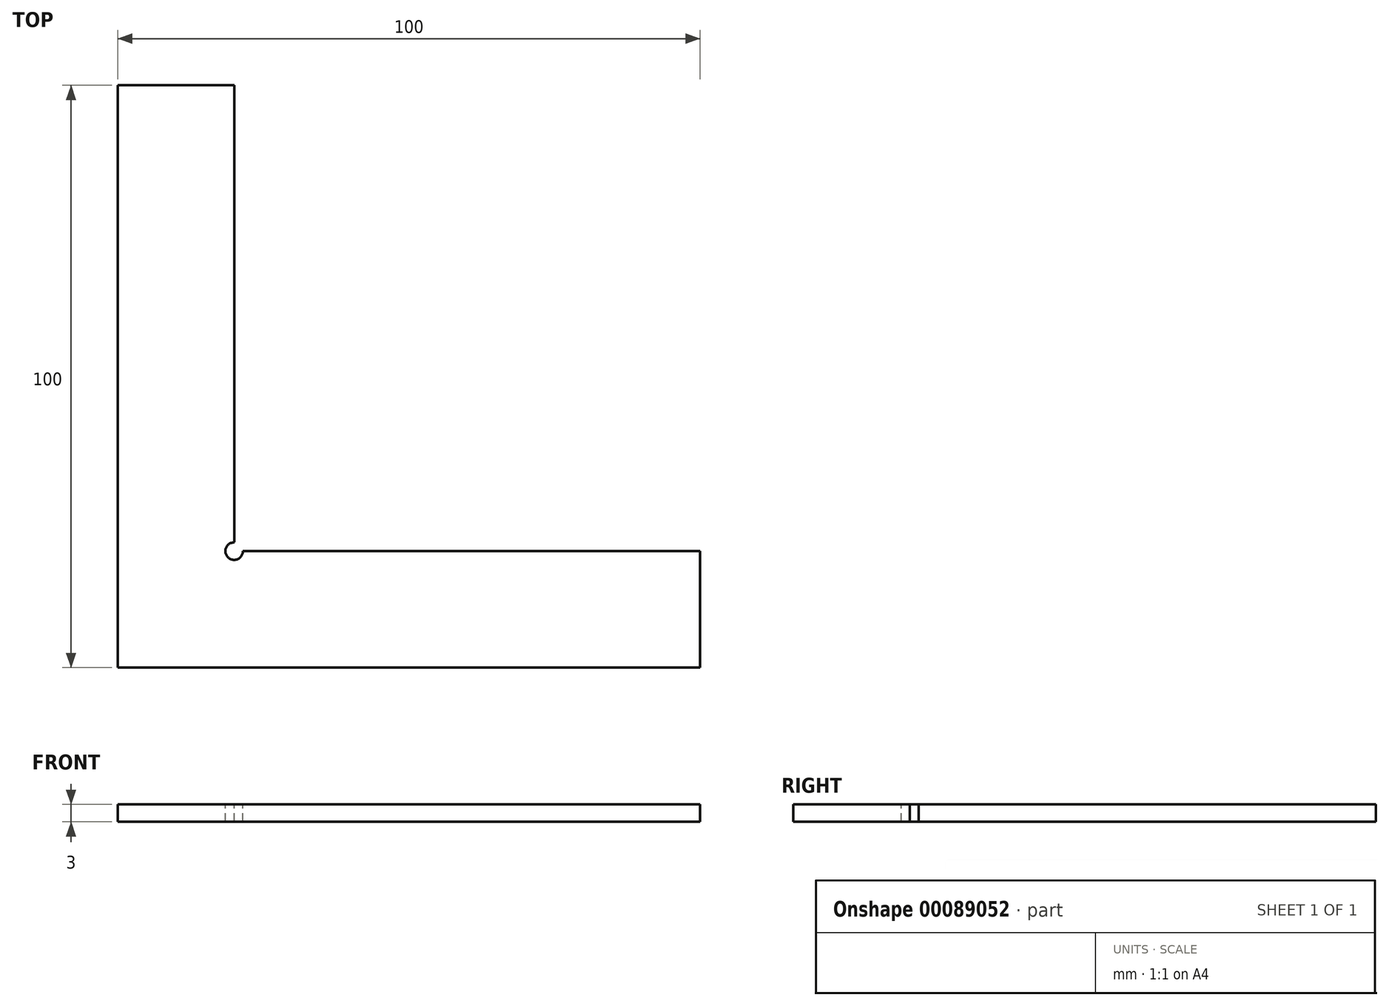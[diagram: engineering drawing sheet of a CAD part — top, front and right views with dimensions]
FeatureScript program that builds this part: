
annotation { "Feature Type Name" : "Feature", "Feature Type Description" : "" }
export const myFeature = defineFeature(function(context is Context, id is Id, definition is map)
    precondition{}
    {
        {
            var Q0;
            Q0=qCreatedBy(makeId("Top.planeOp"),FACE);
            var sketch = newSketch(context, id + "F0", { "sketchPlane" : qUnion([Q0])});
            skLineSegment(sketch, "E0", {"start": v(0, 0) * mm, "end": v(100, 0) * mm});
            skLineSegment(sketch, "E1", {"start": v(100, 0) * mm, "end": v(100, 20) * mm});
            skLineSegment(sketch, "E2", {"start": v(100, 20) * mm, "end": v(22, 20) * mm});
            skLineSegment(sketch, "E3", {"start": v(20, 20) * mm, "end": v(20, 22) * mm});
            skLineSegment(sketch, "E4", {"start": v(20, 100) * mm, "end": v(0, 100) * mm});
            skLineSegment(sketch, "E5", {"start": v(0, 100) * mm, "end": v(0, 0) * mm});
            skArc(sketch, "E6", {"start": v(20, 21.5) * mm, "mid": v(18.94, 18.94) * mm, "end": v(21.5, 20) * mm});
            skLineSegment(sketch, "E7", {"start": v(20, 18.5) * mm, "end": v(20, 15) * mm});
            skLineSegment(sketch, "E8", {"start": v(21, 20) * mm, "end": v(21, 19) * mm});
            skLineSegment(sketch, "E9.1.0.0", {"start": v(22, 20) * mm, "end": v(22, 19) * mm});
            skLineSegment(sketch, "E9.2.0.0", {"start": v(23, 20) * mm, "end": v(23, 19) * mm});
            skLineSegment(sketch, "E9.3.0.0", {"start": v(24, 20) * mm, "end": v(24, 19) * mm});
            skLineSegment(sketch, "E9.direction1", {"start": v(21, 19) * mm, "end": v(22, 19) * mm, "construction": true});
            skLineSegment(sketch, "E10.1.0.0", {"start": v(25, 20) * mm, "end": v(25, 15) * mm});
            skLineSegment(sketch, "E10.1.0.1", {"start": v(26, 20) * mm, "end": v(26, 19) * mm});
            skLineSegment(sketch, "E10.1.0.2", {"start": v(27, 20) * mm, "end": v(27, 19) * mm});
            skLineSegment(sketch, "E10.1.0.3", {"start": v(28, 20) * mm, "end": v(28, 19) * mm});
            skLineSegment(sketch, "E10.1.0.4", {"start": v(29, 20) * mm, "end": v(29, 19) * mm});
            skLineSegment(sketch, "E10.2.0.0", {"start": v(30, 20) * mm, "end": v(30, 15) * mm});
            skLineSegment(sketch, "E10.2.0.1", {"start": v(31, 20) * mm, "end": v(31, 19) * mm});
            skLineSegment(sketch, "E10.2.0.2", {"start": v(32, 20) * mm, "end": v(32, 19) * mm});
            skLineSegment(sketch, "E10.2.0.3", {"start": v(33, 20) * mm, "end": v(33, 19) * mm});
            skLineSegment(sketch, "E10.2.0.4", {"start": v(34, 20) * mm, "end": v(34, 19) * mm});
            skLineSegment(sketch, "E10.3.0.0", {"start": v(35, 20) * mm, "end": v(35, 15) * mm});
            skLineSegment(sketch, "E10.3.0.1", {"start": v(36, 20) * mm, "end": v(36, 19) * mm});
            skLineSegment(sketch, "E10.3.0.2", {"start": v(37, 20) * mm, "end": v(37, 19) * mm});
            skLineSegment(sketch, "E10.3.0.3", {"start": v(38, 20) * mm, "end": v(38, 19) * mm});
            skLineSegment(sketch, "E10.3.0.4", {"start": v(39, 20) * mm, "end": v(39, 19) * mm});
            skLineSegment(sketch, "E10.4.0.0", {"start": v(40, 20) * mm, "end": v(40, 15) * mm});
            skLineSegment(sketch, "E10.4.0.1", {"start": v(41, 20) * mm, "end": v(41, 19) * mm});
            skLineSegment(sketch, "E10.4.0.2", {"start": v(42, 20) * mm, "end": v(42, 19) * mm});
            skLineSegment(sketch, "E10.4.0.3", {"start": v(43, 20) * mm, "end": v(43, 19) * mm});
            skLineSegment(sketch, "E10.4.0.4", {"start": v(44, 20) * mm, "end": v(44, 19) * mm});
            skLineSegment(sketch, "E10.5.0.0", {"start": v(45, 20) * mm, "end": v(45, 15) * mm});
            skLineSegment(sketch, "E10.5.0.1", {"start": v(46, 20) * mm, "end": v(46, 19) * mm});
            skLineSegment(sketch, "E10.5.0.2", {"start": v(47, 20) * mm, "end": v(47, 19) * mm});
            skLineSegment(sketch, "E10.5.0.3", {"start": v(48, 20) * mm, "end": v(48, 19) * mm});
            skLineSegment(sketch, "E10.5.0.4", {"start": v(49, 20) * mm, "end": v(49, 19) * mm});
            skLineSegment(sketch, "E10.6.0.0", {"start": v(50, 20) * mm, "end": v(50, 15) * mm});
            skLineSegment(sketch, "E10.6.0.1", {"start": v(51, 20) * mm, "end": v(51, 19) * mm});
            skLineSegment(sketch, "E10.6.0.2", {"start": v(52, 20) * mm, "end": v(52, 19) * mm});
            skLineSegment(sketch, "E10.6.0.3", {"start": v(53, 20) * mm, "end": v(53, 19) * mm});
            skLineSegment(sketch, "E10.6.0.4", {"start": v(54, 20) * mm, "end": v(54, 19) * mm});
            skLineSegment(sketch, "E10.7.0.0", {"start": v(55, 20) * mm, "end": v(55, 15) * mm});
            skLineSegment(sketch, "E10.7.0.1", {"start": v(56, 20) * mm, "end": v(56, 19) * mm});
            skLineSegment(sketch, "E10.7.0.2", {"start": v(57, 20) * mm, "end": v(57, 19) * mm});
            skLineSegment(sketch, "E10.7.0.3", {"start": v(58, 20) * mm, "end": v(58, 19) * mm});
            skLineSegment(sketch, "E10.7.0.4", {"start": v(59, 20) * mm, "end": v(59, 19) * mm});
            skLineSegment(sketch, "E10.8.0.0", {"start": v(60, 20) * mm, "end": v(60, 15) * mm});
            skLineSegment(sketch, "E10.8.0.1", {"start": v(61, 20) * mm, "end": v(61, 19) * mm});
            skLineSegment(sketch, "E10.8.0.2", {"start": v(62, 20) * mm, "end": v(62, 19) * mm});
            skLineSegment(sketch, "E10.8.0.3", {"start": v(63, 20) * mm, "end": v(63, 19) * mm});
            skLineSegment(sketch, "E10.8.0.4", {"start": v(64, 20) * mm, "end": v(64, 19) * mm});
            skLineSegment(sketch, "E10.9.0.0", {"start": v(65, 20) * mm, "end": v(65, 15) * mm});
            skLineSegment(sketch, "E10.9.0.1", {"start": v(66, 20) * mm, "end": v(66, 19) * mm});
            skLineSegment(sketch, "E10.9.0.2", {"start": v(67, 20) * mm, "end": v(67, 19) * mm});
            skLineSegment(sketch, "E10.9.0.3", {"start": v(68, 20) * mm, "end": v(68, 19) * mm});
            skLineSegment(sketch, "E10.9.0.4", {"start": v(69, 20) * mm, "end": v(69, 19) * mm});
            skLineSegment(sketch, "E10.10.0.0", {"start": v(70, 20) * mm, "end": v(70, 15) * mm});
            skLineSegment(sketch, "E10.10.0.1", {"start": v(71, 20) * mm, "end": v(71, 19) * mm});
            skLineSegment(sketch, "E10.10.0.2", {"start": v(72, 20) * mm, "end": v(72, 19) * mm});
            skLineSegment(sketch, "E10.10.0.3", {"start": v(73, 20) * mm, "end": v(73, 19) * mm});
            skLineSegment(sketch, "E10.10.0.4", {"start": v(74, 20) * mm, "end": v(74, 19) * mm});
            skLineSegment(sketch, "E10.11.0.0", {"start": v(75, 20) * mm, "end": v(75, 15) * mm});
            skLineSegment(sketch, "E10.11.0.1", {"start": v(76, 20) * mm, "end": v(76, 19) * mm});
            skLineSegment(sketch, "E10.11.0.2", {"start": v(77, 20) * mm, "end": v(77, 19) * mm});
            skLineSegment(sketch, "E10.11.0.3", {"start": v(78, 20) * mm, "end": v(78, 19) * mm});
            skLineSegment(sketch, "E10.11.0.4", {"start": v(79, 20) * mm, "end": v(79, 19) * mm});
            skLineSegment(sketch, "E10.12.0.0", {"start": v(80, 20) * mm, "end": v(80, 15) * mm});
            skLineSegment(sketch, "E10.12.0.1", {"start": v(81, 20) * mm, "end": v(81, 19) * mm});
            skLineSegment(sketch, "E10.12.0.2", {"start": v(82, 20) * mm, "end": v(82, 19) * mm});
            skLineSegment(sketch, "E10.12.0.3", {"start": v(83, 20) * mm, "end": v(83, 19) * mm});
            skLineSegment(sketch, "E10.12.0.4", {"start": v(84, 20) * mm, "end": v(84, 19) * mm});
            skLineSegment(sketch, "E10.13.0.0", {"start": v(85, 20) * mm, "end": v(85, 15) * mm});
            skLineSegment(sketch, "E10.13.0.1", {"start": v(86, 20) * mm, "end": v(86, 19) * mm});
            skLineSegment(sketch, "E10.13.0.2", {"start": v(87, 20) * mm, "end": v(87, 19) * mm});
            skLineSegment(sketch, "E10.13.0.3", {"start": v(88, 20) * mm, "end": v(88, 19) * mm});
            skLineSegment(sketch, "E10.13.0.4", {"start": v(89, 20) * mm, "end": v(89, 19) * mm});
            skLineSegment(sketch, "E10.14.0.0", {"start": v(90, 20) * mm, "end": v(90, 15) * mm});
            skLineSegment(sketch, "E10.14.0.1", {"start": v(91, 20) * mm, "end": v(91, 19) * mm});
            skLineSegment(sketch, "E10.14.0.2", {"start": v(92, 20) * mm, "end": v(92, 19) * mm});
            skLineSegment(sketch, "E10.14.0.3", {"start": v(93, 20) * mm, "end": v(93, 19) * mm});
            skLineSegment(sketch, "E10.14.0.4", {"start": v(94, 20) * mm, "end": v(94, 19) * mm});
            skLineSegment(sketch, "E10.direction1", {"start": v(20, 15) * mm, "end": v(25, 15) * mm, "construction": true});
            skLineSegment(sketch, "E11.0.15.0", {"start": v(95, 20) * mm, "end": v(95, 15) * mm});
            skLineSegment(sketch, "E11.3.15.0", {"start": v(96, 20) * mm, "end": v(96, 19) * mm});
            skLineSegment(sketch, "E11.6.15.0", {"start": v(97, 20) * mm, "end": v(97, 19) * mm});
            skLineSegment(sketch, "E11.9.15.0", {"start": v(98, 20) * mm, "end": v(98, 19) * mm});
            skLineSegment(sketch, "E11.12.15.0", {"start": v(99, 20) * mm, "end": v(99, 19) * mm});
            skLineSegment(sketch, "E12", {"start": v(18.5, 20) * mm, "end": v(15, 20) * mm});
            skLineSegment(sketch, "E13", {"start": v(20, 21) * mm, "end": v(19, 21) * mm});
            skLineSegment(sketch, "E14.1.0.0", {"start": v(20, 22) * mm, "end": v(19, 22) * mm});
            skLineSegment(sketch, "E14.2.0.0", {"start": v(20, 23) * mm, "end": v(19, 23) * mm});
            skLineSegment(sketch, "E14.3.0.0", {"start": v(20, 24) * mm, "end": v(19, 24) * mm});
            skLineSegment(sketch, "E14.direction1", {"start": v(19, 21) * mm, "end": v(19, 22) * mm, "construction": true});
            skLineSegment(sketch, "E15.1.0.0", {"start": v(20, 25) * mm, "end": v(15, 25) * mm});
            skLineSegment(sketch, "E15.1.0.1", {"start": v(20, 26) * mm, "end": v(19, 26) * mm});
            skLineSegment(sketch, "E15.1.0.2", {"start": v(20, 27) * mm, "end": v(19, 27) * mm});
            skLineSegment(sketch, "E15.1.0.3", {"start": v(20, 28) * mm, "end": v(19, 28) * mm});
            skLineSegment(sketch, "E15.1.0.4", {"start": v(20, 29) * mm, "end": v(19, 29) * mm});
            skLineSegment(sketch, "E15.2.0.0", {"start": v(20, 30) * mm, "end": v(15, 30) * mm});
            skLineSegment(sketch, "E15.2.0.1", {"start": v(20, 31) * mm, "end": v(19, 31) * mm});
            skLineSegment(sketch, "E15.2.0.2", {"start": v(20, 32) * mm, "end": v(19, 32) * mm});
            skLineSegment(sketch, "E15.2.0.3", {"start": v(20, 33) * mm, "end": v(19, 33) * mm});
            skLineSegment(sketch, "E15.2.0.4", {"start": v(20, 34) * mm, "end": v(19, 34) * mm});
            skLineSegment(sketch, "E15.3.0.0", {"start": v(20, 35) * mm, "end": v(15, 35) * mm});
            skLineSegment(sketch, "E15.3.0.1", {"start": v(20, 36) * mm, "end": v(19, 36) * mm});
            skLineSegment(sketch, "E15.3.0.2", {"start": v(20, 37) * mm, "end": v(19, 37) * mm});
            skLineSegment(sketch, "E15.3.0.3", {"start": v(20, 38) * mm, "end": v(19, 38) * mm});
            skLineSegment(sketch, "E15.3.0.4", {"start": v(20, 39) * mm, "end": v(19, 39) * mm});
            skLineSegment(sketch, "E15.4.0.0", {"start": v(20, 40) * mm, "end": v(15, 40) * mm});
            skLineSegment(sketch, "E15.4.0.1", {"start": v(20, 41) * mm, "end": v(19, 41) * mm});
            skLineSegment(sketch, "E15.4.0.2", {"start": v(20, 42) * mm, "end": v(19, 42) * mm});
            skLineSegment(sketch, "E15.4.0.3", {"start": v(20, 43) * mm, "end": v(19, 43) * mm});
            skLineSegment(sketch, "E15.4.0.4", {"start": v(20, 44) * mm, "end": v(19, 44) * mm});
            skLineSegment(sketch, "E15.5.0.0", {"start": v(20, 45) * mm, "end": v(15, 45) * mm});
            skLineSegment(sketch, "E15.5.0.1", {"start": v(20, 46) * mm, "end": v(19, 46) * mm});
            skLineSegment(sketch, "E15.5.0.2", {"start": v(20, 47) * mm, "end": v(19, 47) * mm});
            skLineSegment(sketch, "E15.5.0.3", {"start": v(20, 48) * mm, "end": v(19, 48) * mm});
            skLineSegment(sketch, "E15.5.0.4", {"start": v(20, 49) * mm, "end": v(19, 49) * mm});
            skLineSegment(sketch, "E15.6.0.0", {"start": v(20, 50) * mm, "end": v(15, 50) * mm});
            skLineSegment(sketch, "E15.6.0.1", {"start": v(20, 51) * mm, "end": v(19, 51) * mm});
            skLineSegment(sketch, "E15.6.0.2", {"start": v(20, 52) * mm, "end": v(19, 52) * mm});
            skLineSegment(sketch, "E15.6.0.3", {"start": v(20, 53) * mm, "end": v(19, 53) * mm});
            skLineSegment(sketch, "E15.6.0.4", {"start": v(20, 54) * mm, "end": v(19, 54) * mm});
            skLineSegment(sketch, "E15.7.0.0", {"start": v(20, 55) * mm, "end": v(15, 55) * mm});
            skLineSegment(sketch, "E15.7.0.1", {"start": v(20, 56) * mm, "end": v(19, 56) * mm});
            skLineSegment(sketch, "E15.7.0.2", {"start": v(20, 57) * mm, "end": v(19, 57) * mm});
            skLineSegment(sketch, "E15.7.0.3", {"start": v(20, 58) * mm, "end": v(19, 58) * mm});
            skLineSegment(sketch, "E15.7.0.4", {"start": v(20, 59) * mm, "end": v(19, 59) * mm});
            skLineSegment(sketch, "E15.8.0.0", {"start": v(20, 60) * mm, "end": v(15, 60) * mm});
            skLineSegment(sketch, "E15.8.0.1", {"start": v(20, 61) * mm, "end": v(19, 61) * mm});
            skLineSegment(sketch, "E15.8.0.2", {"start": v(20, 62) * mm, "end": v(19, 62) * mm});
            skLineSegment(sketch, "E15.8.0.3", {"start": v(20, 63) * mm, "end": v(19, 63) * mm});
            skLineSegment(sketch, "E15.8.0.4", {"start": v(20, 64) * mm, "end": v(19, 64) * mm});
            skLineSegment(sketch, "E15.9.0.0", {"start": v(20, 65) * mm, "end": v(15, 65) * mm});
            skLineSegment(sketch, "E15.9.0.1", {"start": v(20, 66) * mm, "end": v(19, 66) * mm});
            skLineSegment(sketch, "E15.9.0.2", {"start": v(20, 67) * mm, "end": v(19, 67) * mm});
            skLineSegment(sketch, "E15.9.0.3", {"start": v(20, 68) * mm, "end": v(19, 68) * mm});
            skLineSegment(sketch, "E15.9.0.4", {"start": v(20, 69) * mm, "end": v(19, 69) * mm});
            skLineSegment(sketch, "E15.10.0.0", {"start": v(20, 70) * mm, "end": v(15, 70) * mm});
            skLineSegment(sketch, "E15.10.0.1", {"start": v(20, 71) * mm, "end": v(19, 71) * mm});
            skLineSegment(sketch, "E15.10.0.2", {"start": v(20, 72) * mm, "end": v(19, 72) * mm});
            skLineSegment(sketch, "E15.10.0.3", {"start": v(20, 73) * mm, "end": v(19, 73) * mm});
            skLineSegment(sketch, "E15.10.0.4", {"start": v(20, 74) * mm, "end": v(19, 74) * mm});
            skLineSegment(sketch, "E15.11.0.0", {"start": v(20, 75) * mm, "end": v(15, 75) * mm});
            skLineSegment(sketch, "E15.11.0.1", {"start": v(20, 76) * mm, "end": v(19, 76) * mm});
            skLineSegment(sketch, "E15.11.0.2", {"start": v(20, 77) * mm, "end": v(19, 77) * mm});
            skLineSegment(sketch, "E15.11.0.3", {"start": v(20, 78) * mm, "end": v(19, 78) * mm});
            skLineSegment(sketch, "E15.11.0.4", {"start": v(20, 79) * mm, "end": v(19, 79) * mm});
            skLineSegment(sketch, "E15.12.0.0", {"start": v(20, 80) * mm, "end": v(15, 80) * mm});
            skLineSegment(sketch, "E15.12.0.1", {"start": v(20, 81) * mm, "end": v(19, 81) * mm});
            skLineSegment(sketch, "E15.12.0.2", {"start": v(20, 82) * mm, "end": v(19, 82) * mm});
            skLineSegment(sketch, "E15.12.0.3", {"start": v(20, 83) * mm, "end": v(19, 83) * mm});
            skLineSegment(sketch, "E15.12.0.4", {"start": v(20, 84) * mm, "end": v(19, 84) * mm});
            skLineSegment(sketch, "E15.13.0.0", {"start": v(20, 85) * mm, "end": v(15, 85) * mm});
            skLineSegment(sketch, "E15.13.0.1", {"start": v(20, 86) * mm, "end": v(19, 86) * mm});
            skLineSegment(sketch, "E15.13.0.2", {"start": v(20, 87) * mm, "end": v(19, 87) * mm});
            skLineSegment(sketch, "E15.13.0.3", {"start": v(20, 88) * mm, "end": v(19, 88) * mm});
            skLineSegment(sketch, "E15.13.0.4", {"start": v(20, 89) * mm, "end": v(19, 89) * mm});
            skLineSegment(sketch, "E15.14.0.0", {"start": v(20, 90) * mm, "end": v(15, 90) * mm});
            skLineSegment(sketch, "E15.14.0.1", {"start": v(20, 91) * mm, "end": v(19, 91) * mm});
            skLineSegment(sketch, "E15.14.0.2", {"start": v(20, 92) * mm, "end": v(19, 92) * mm});
            skLineSegment(sketch, "E15.14.0.3", {"start": v(20, 93) * mm, "end": v(19, 93) * mm});
            skLineSegment(sketch, "E15.14.0.4", {"start": v(20, 94) * mm, "end": v(19, 94) * mm});
            skLineSegment(sketch, "E15.15.0.0", {"start": v(20, 95) * mm, "end": v(15, 95) * mm});
            skLineSegment(sketch, "E15.15.0.1", {"start": v(20, 96) * mm, "end": v(19, 96) * mm});
            skLineSegment(sketch, "E15.15.0.2", {"start": v(20, 97) * mm, "end": v(19, 97) * mm});
            skLineSegment(sketch, "E15.15.0.3", {"start": v(20, 98) * mm, "end": v(19, 98) * mm});
            skLineSegment(sketch, "E15.15.0.4", {"start": v(20, 99) * mm, "end": v(19, 99) * mm});
            skLineSegment(sketch, "E15.direction1", {"start": v(15, 20) * mm, "end": v(15, 25) * mm, "construction": true});
            skLineSegment(sketch, "E16.trimOffspring", {"start": v(20, 23) * mm, "end": v(20, 100) * mm});
            skLineSegment(sketch, "E17.trimOffspring", {"start": v(21, 20) * mm, "end": v(20, 20) * mm});
            skLineSegment(sketch, "E18", {"start": v(20, 23) * mm, "end": v(20, 22) * mm});
            skLineSegment(sketch, "E19", {"start": v(21, 20) * mm, "end": v(22, 20) * mm});
            skLineSegment(sketch, "E20", {"start": v(1, 0) * mm, "end": v(1, 1) * mm});
            skLineSegment(sketch, "E21.1.0.0", {"start": v(2, 0) * mm, "end": v(2, 1) * mm});
            skLineSegment(sketch, "E21.2.0.0", {"start": v(3, 0) * mm, "end": v(3, 1) * mm});
            skLineSegment(sketch, "E21.3.0.0", {"start": v(4, 0) * mm, "end": v(4, 1) * mm});
            skLineSegment(sketch, "E21.direction1", {"start": v(1, 0) * mm, "end": v(2, 0) * mm, "construction": true});
            skLineSegment(sketch, "E22", {"start": v(5, 0) * mm, "end": v(5, 5) * mm});
            skLineSegment(sketch, "E23.1.0.0", {"start": v(6, 0) * mm, "end": v(6, 1) * mm});
            skLineSegment(sketch, "E23.1.0.1", {"start": v(7, 0) * mm, "end": v(7, 1) * mm});
            skLineSegment(sketch, "E23.1.0.2", {"start": v(8, 0) * mm, "end": v(8, 1) * mm});
            skLineSegment(sketch, "E23.1.0.3", {"start": v(9, 0) * mm, "end": v(9, 1) * mm});
            skLineSegment(sketch, "E23.1.0.4", {"start": v(10, 0) * mm, "end": v(10, 5) * mm});
            skLineSegment(sketch, "E23.2.0.0", {"start": v(11, 0) * mm, "end": v(11, 1) * mm});
            skLineSegment(sketch, "E23.2.0.1", {"start": v(12, 0) * mm, "end": v(12, 1) * mm});
            skLineSegment(sketch, "E23.2.0.2", {"start": v(13, 0) * mm, "end": v(13, 1) * mm});
            skLineSegment(sketch, "E23.2.0.3", {"start": v(14, 0) * mm, "end": v(14, 1) * mm});
            skLineSegment(sketch, "E23.2.0.4", {"start": v(15, 0) * mm, "end": v(15, 5) * mm});
            skLineSegment(sketch, "E23.3.0.0", {"start": v(16, 0) * mm, "end": v(16, 1) * mm});
            skLineSegment(sketch, "E23.3.0.1", {"start": v(17, 0) * mm, "end": v(17, 1) * mm});
            skLineSegment(sketch, "E23.3.0.2", {"start": v(18, 0) * mm, "end": v(18, 1) * mm});
            skLineSegment(sketch, "E23.3.0.3", {"start": v(19, 0) * mm, "end": v(19, 1) * mm});
            skLineSegment(sketch, "E23.3.0.4", {"start": v(20, 0) * mm, "end": v(20, 5) * mm});
            skLineSegment(sketch, "E23.4.0.0", {"start": v(21, 0) * mm, "end": v(21, 1) * mm});
            skLineSegment(sketch, "E23.4.0.1", {"start": v(22, 0) * mm, "end": v(22, 1) * mm});
            skLineSegment(sketch, "E23.4.0.2", {"start": v(23, 0) * mm, "end": v(23, 1) * mm});
            skLineSegment(sketch, "E23.4.0.3", {"start": v(24, 0) * mm, "end": v(24, 1) * mm});
            skLineSegment(sketch, "E23.4.0.4", {"start": v(25, 0) * mm, "end": v(25, 5) * mm});
            skLineSegment(sketch, "E23.5.0.0", {"start": v(26, 0) * mm, "end": v(26, 1) * mm});
            skLineSegment(sketch, "E23.5.0.1", {"start": v(27, 0) * mm, "end": v(27, 1) * mm});
            skLineSegment(sketch, "E23.5.0.2", {"start": v(28, 0) * mm, "end": v(28, 1) * mm});
            skLineSegment(sketch, "E23.5.0.3", {"start": v(29, 0) * mm, "end": v(29, 1) * mm});
            skLineSegment(sketch, "E23.5.0.4", {"start": v(30, 0) * mm, "end": v(30, 5) * mm});
            skLineSegment(sketch, "E23.6.0.0", {"start": v(31, 0) * mm, "end": v(31, 1) * mm});
            skLineSegment(sketch, "E23.6.0.1", {"start": v(32, 0) * mm, "end": v(32, 1) * mm});
            skLineSegment(sketch, "E23.6.0.2", {"start": v(33, 0) * mm, "end": v(33, 1) * mm});
            skLineSegment(sketch, "E23.6.0.3", {"start": v(34, 0) * mm, "end": v(34, 1) * mm});
            skLineSegment(sketch, "E23.6.0.4", {"start": v(35, 0) * mm, "end": v(35, 5) * mm});
            skLineSegment(sketch, "E23.7.0.0", {"start": v(36, 0) * mm, "end": v(36, 1) * mm});
            skLineSegment(sketch, "E23.7.0.1", {"start": v(37, 0) * mm, "end": v(37, 1) * mm});
            skLineSegment(sketch, "E23.7.0.2", {"start": v(38, 0) * mm, "end": v(38, 1) * mm});
            skLineSegment(sketch, "E23.7.0.3", {"start": v(39, 0) * mm, "end": v(39, 1) * mm});
            skLineSegment(sketch, "E23.7.0.4", {"start": v(40, 0) * mm, "end": v(40, 5) * mm});
            skLineSegment(sketch, "E23.8.0.0", {"start": v(41, 0) * mm, "end": v(41, 1) * mm});
            skLineSegment(sketch, "E23.8.0.1", {"start": v(42, 0) * mm, "end": v(42, 1) * mm});
            skLineSegment(sketch, "E23.8.0.2", {"start": v(43, 0) * mm, "end": v(43, 1) * mm});
            skLineSegment(sketch, "E23.8.0.3", {"start": v(44, 0) * mm, "end": v(44, 1) * mm});
            skLineSegment(sketch, "E23.8.0.4", {"start": v(45, 0) * mm, "end": v(45, 5) * mm});
            skLineSegment(sketch, "E23.9.0.0", {"start": v(46, 0) * mm, "end": v(46, 1) * mm});
            skLineSegment(sketch, "E23.9.0.1", {"start": v(47, 0) * mm, "end": v(47, 1) * mm});
            skLineSegment(sketch, "E23.9.0.2", {"start": v(48, 0) * mm, "end": v(48, 1) * mm});
            skLineSegment(sketch, "E23.9.0.3", {"start": v(49, 0) * mm, "end": v(49, 1) * mm});
            skLineSegment(sketch, "E23.9.0.4", {"start": v(50, 0) * mm, "end": v(50, 5) * mm});
            skLineSegment(sketch, "E23.10.0.0", {"start": v(51, 0) * mm, "end": v(51, 1) * mm});
            skLineSegment(sketch, "E23.10.0.1", {"start": v(52, 0) * mm, "end": v(52, 1) * mm});
            skLineSegment(sketch, "E23.10.0.2", {"start": v(53, 0) * mm, "end": v(53, 1) * mm});
            skLineSegment(sketch, "E23.10.0.3", {"start": v(54, 0) * mm, "end": v(54, 1) * mm});
            skLineSegment(sketch, "E23.10.0.4", {"start": v(55, 0) * mm, "end": v(55, 5) * mm});
            skLineSegment(sketch, "E23.11.0.0", {"start": v(56, 0) * mm, "end": v(56, 1) * mm});
            skLineSegment(sketch, "E23.11.0.1", {"start": v(57, 0) * mm, "end": v(57, 1) * mm});
            skLineSegment(sketch, "E23.11.0.2", {"start": v(58, 0) * mm, "end": v(58, 1) * mm});
            skLineSegment(sketch, "E23.11.0.3", {"start": v(59, 0) * mm, "end": v(59, 1) * mm});
            skLineSegment(sketch, "E23.11.0.4", {"start": v(60, 0) * mm, "end": v(60, 5) * mm});
            skLineSegment(sketch, "E23.12.0.0", {"start": v(61, 0) * mm, "end": v(61, 1) * mm});
            skLineSegment(sketch, "E23.12.0.1", {"start": v(62, 0) * mm, "end": v(62, 1) * mm});
            skLineSegment(sketch, "E23.12.0.2", {"start": v(63, 0) * mm, "end": v(63, 1) * mm});
            skLineSegment(sketch, "E23.12.0.3", {"start": v(64, 0) * mm, "end": v(64, 1) * mm});
            skLineSegment(sketch, "E23.12.0.4", {"start": v(65, 0) * mm, "end": v(65, 5) * mm});
            skLineSegment(sketch, "E23.13.0.0", {"start": v(66, 0) * mm, "end": v(66, 1) * mm});
            skLineSegment(sketch, "E23.13.0.1", {"start": v(67, 0) * mm, "end": v(67, 1) * mm});
            skLineSegment(sketch, "E23.13.0.2", {"start": v(68, 0) * mm, "end": v(68, 1) * mm});
            skLineSegment(sketch, "E23.13.0.3", {"start": v(69, 0) * mm, "end": v(69, 1) * mm});
            skLineSegment(sketch, "E23.13.0.4", {"start": v(70, 0) * mm, "end": v(70, 5) * mm});
            skLineSegment(sketch, "E23.14.0.0", {"start": v(71, 0) * mm, "end": v(71, 1) * mm});
            skLineSegment(sketch, "E23.14.0.1", {"start": v(72, 0) * mm, "end": v(72, 1) * mm});
            skLineSegment(sketch, "E23.14.0.2", {"start": v(73, 0) * mm, "end": v(73, 1) * mm});
            skLineSegment(sketch, "E23.14.0.3", {"start": v(74, 0) * mm, "end": v(74, 1) * mm});
            skLineSegment(sketch, "E23.14.0.4", {"start": v(75, 0) * mm, "end": v(75, 5) * mm});
            skLineSegment(sketch, "E23.15.0.0", {"start": v(76, 0) * mm, "end": v(76, 1) * mm});
            skLineSegment(sketch, "E23.15.0.1", {"start": v(77, 0) * mm, "end": v(77, 1) * mm});
            skLineSegment(sketch, "E23.15.0.2", {"start": v(78, 0) * mm, "end": v(78, 1) * mm});
            skLineSegment(sketch, "E23.15.0.3", {"start": v(79, 0) * mm, "end": v(79, 1) * mm});
            skLineSegment(sketch, "E23.15.0.4", {"start": v(80, 0) * mm, "end": v(80, 5) * mm});
            skLineSegment(sketch, "E23.16.0.0", {"start": v(81, 0) * mm, "end": v(81, 1) * mm});
            skLineSegment(sketch, "E23.16.0.1", {"start": v(82, 0) * mm, "end": v(82, 1) * mm});
            skLineSegment(sketch, "E23.16.0.2", {"start": v(83, 0) * mm, "end": v(83, 1) * mm});
            skLineSegment(sketch, "E23.16.0.3", {"start": v(84, 0) * mm, "end": v(84, 1) * mm});
            skLineSegment(sketch, "E23.16.0.4", {"start": v(85, 0) * mm, "end": v(85, 5) * mm});
            skLineSegment(sketch, "E23.17.0.0", {"start": v(86, 0) * mm, "end": v(86, 1) * mm});
            skLineSegment(sketch, "E23.17.0.1", {"start": v(87, 0) * mm, "end": v(87, 1) * mm});
            skLineSegment(sketch, "E23.17.0.2", {"start": v(88, 0) * mm, "end": v(88, 1) * mm});
            skLineSegment(sketch, "E23.17.0.3", {"start": v(89, 0) * mm, "end": v(89, 1) * mm});
            skLineSegment(sketch, "E23.17.0.4", {"start": v(90, 0) * mm, "end": v(90, 5) * mm});
            skLineSegment(sketch, "E23.18.0.0", {"start": v(91, 0) * mm, "end": v(91, 1) * mm});
            skLineSegment(sketch, "E23.18.0.1", {"start": v(92, 0) * mm, "end": v(92, 1) * mm});
            skLineSegment(sketch, "E23.18.0.2", {"start": v(93, 0) * mm, "end": v(93, 1) * mm});
            skLineSegment(sketch, "E23.18.0.3", {"start": v(94, 0) * mm, "end": v(94, 1) * mm});
            skLineSegment(sketch, "E23.18.0.4", {"start": v(95, 0) * mm, "end": v(95, 5) * mm});
            skLineSegment(sketch, "E23.19.0.0", {"start": v(96, 0) * mm, "end": v(96, 1) * mm});
            skLineSegment(sketch, "E23.19.0.1", {"start": v(97, 0) * mm, "end": v(97, 1) * mm});
            skLineSegment(sketch, "E23.19.0.2", {"start": v(98, 0) * mm, "end": v(98, 1) * mm});
            skLineSegment(sketch, "E23.19.0.3", {"start": v(99, 0) * mm, "end": v(99, 1) * mm});
            skLineSegment(sketch, "E23.19.0.4", {"start": v(100, 0) * mm, "end": v(100, 5) * mm});
            skLineSegment(sketch, "E23.direction1", {"start": v(1, 0) * mm, "end": v(6, 0) * mm, "construction": true});
            skLineSegment(sketch, "E24", {"start": v(0, 1) * mm, "end": v(1, 1) * mm});
            skLineSegment(sketch, "E25.1.0.0", {"start": v(0, 2) * mm, "end": v(1, 2) * mm});
            skLineSegment(sketch, "E25.2.0.0", {"start": v(0, 3) * mm, "end": v(1, 3) * mm});
            skLineSegment(sketch, "E25.3.0.0", {"start": v(0, 4) * mm, "end": v(1, 4) * mm});
            skLineSegment(sketch, "E25.direction1", {"start": v(0, 1) * mm, "end": v(0, 2) * mm, "construction": true});
            skLineSegment(sketch, "E26", {"start": v(0, 5) * mm, "end": v(5, 5) * mm});
            skLineSegment(sketch, "E27.1.0.0", {"start": v(0, 6) * mm, "end": v(1, 6) * mm});
            skLineSegment(sketch, "E27.1.0.1", {"start": v(0, 7) * mm, "end": v(1, 7) * mm});
            skLineSegment(sketch, "E27.1.0.2", {"start": v(0, 8) * mm, "end": v(1, 8) * mm});
            skLineSegment(sketch, "E27.1.0.3", {"start": v(0, 9) * mm, "end": v(1, 9) * mm});
            skLineSegment(sketch, "E27.1.0.4", {"start": v(0, 10) * mm, "end": v(5, 10) * mm});
            skLineSegment(sketch, "E27.2.0.0", {"start": v(0, 11) * mm, "end": v(1, 11) * mm});
            skLineSegment(sketch, "E27.2.0.1", {"start": v(0, 12) * mm, "end": v(1, 12) * mm});
            skLineSegment(sketch, "E27.2.0.2", {"start": v(0, 13) * mm, "end": v(1, 13) * mm});
            skLineSegment(sketch, "E27.2.0.3", {"start": v(0, 14) * mm, "end": v(1, 14) * mm});
            skLineSegment(sketch, "E27.2.0.4", {"start": v(0, 15) * mm, "end": v(5, 15) * mm});
            skLineSegment(sketch, "E27.3.0.0", {"start": v(0, 16) * mm, "end": v(1, 16) * mm});
            skLineSegment(sketch, "E27.3.0.1", {"start": v(0, 17) * mm, "end": v(1, 17) * mm});
            skLineSegment(sketch, "E27.3.0.2", {"start": v(0, 18) * mm, "end": v(1, 18) * mm});
            skLineSegment(sketch, "E27.3.0.3", {"start": v(0, 19) * mm, "end": v(1, 19) * mm});
            skLineSegment(sketch, "E27.3.0.4", {"start": v(0, 20) * mm, "end": v(5, 20) * mm});
            skLineSegment(sketch, "E27.4.0.0", {"start": v(0, 21) * mm, "end": v(1, 21) * mm});
            skLineSegment(sketch, "E27.4.0.1", {"start": v(0, 22) * mm, "end": v(1, 22) * mm});
            skLineSegment(sketch, "E27.4.0.2", {"start": v(0, 23) * mm, "end": v(1, 23) * mm});
            skLineSegment(sketch, "E27.4.0.3", {"start": v(0, 24) * mm, "end": v(1, 24) * mm});
            skLineSegment(sketch, "E27.4.0.4", {"start": v(0, 25) * mm, "end": v(5, 25) * mm});
            skLineSegment(sketch, "E27.5.0.0", {"start": v(0, 26) * mm, "end": v(1, 26) * mm});
            skLineSegment(sketch, "E27.5.0.1", {"start": v(0, 27) * mm, "end": v(1, 27) * mm});
            skLineSegment(sketch, "E27.5.0.2", {"start": v(0, 28) * mm, "end": v(1, 28) * mm});
            skLineSegment(sketch, "E27.5.0.3", {"start": v(0, 29) * mm, "end": v(1, 29) * mm});
            skLineSegment(sketch, "E27.5.0.4", {"start": v(0, 30) * mm, "end": v(5, 30) * mm});
            skLineSegment(sketch, "E27.6.0.0", {"start": v(0, 31) * mm, "end": v(1, 31) * mm});
            skLineSegment(sketch, "E27.6.0.1", {"start": v(0, 32) * mm, "end": v(1, 32) * mm});
            skLineSegment(sketch, "E27.6.0.2", {"start": v(0, 33) * mm, "end": v(1, 33) * mm});
            skLineSegment(sketch, "E27.6.0.3", {"start": v(0, 34) * mm, "end": v(1, 34) * mm});
            skLineSegment(sketch, "E27.6.0.4", {"start": v(0, 35) * mm, "end": v(5, 35) * mm});
            skLineSegment(sketch, "E27.7.0.0", {"start": v(0, 36) * mm, "end": v(1, 36) * mm});
            skLineSegment(sketch, "E27.7.0.1", {"start": v(0, 37) * mm, "end": v(1, 37) * mm});
            skLineSegment(sketch, "E27.7.0.2", {"start": v(0, 38) * mm, "end": v(1, 38) * mm});
            skLineSegment(sketch, "E27.7.0.3", {"start": v(0, 39) * mm, "end": v(1, 39) * mm});
            skLineSegment(sketch, "E27.7.0.4", {"start": v(0, 40) * mm, "end": v(5, 40) * mm});
            skLineSegment(sketch, "E27.8.0.0", {"start": v(0, 41) * mm, "end": v(1, 41) * mm});
            skLineSegment(sketch, "E27.8.0.1", {"start": v(0, 42) * mm, "end": v(1, 42) * mm});
            skLineSegment(sketch, "E27.8.0.2", {"start": v(0, 43) * mm, "end": v(1, 43) * mm});
            skLineSegment(sketch, "E27.8.0.3", {"start": v(0, 44) * mm, "end": v(1, 44) * mm});
            skLineSegment(sketch, "E27.8.0.4", {"start": v(0, 45) * mm, "end": v(5, 45) * mm});
            skLineSegment(sketch, "E27.9.0.0", {"start": v(0, 46) * mm, "end": v(1, 46) * mm});
            skLineSegment(sketch, "E27.9.0.1", {"start": v(0, 47) * mm, "end": v(1, 47) * mm});
            skLineSegment(sketch, "E27.9.0.2", {"start": v(0, 48) * mm, "end": v(1, 48) * mm});
            skLineSegment(sketch, "E27.9.0.3", {"start": v(0, 49) * mm, "end": v(1, 49) * mm});
            skLineSegment(sketch, "E27.9.0.4", {"start": v(0, 50) * mm, "end": v(5, 50) * mm});
            skLineSegment(sketch, "E27.10.0.0", {"start": v(0, 51) * mm, "end": v(1, 51) * mm});
            skLineSegment(sketch, "E27.10.0.1", {"start": v(0, 52) * mm, "end": v(1, 52) * mm});
            skLineSegment(sketch, "E27.10.0.2", {"start": v(0, 53) * mm, "end": v(1, 53) * mm});
            skLineSegment(sketch, "E27.10.0.3", {"start": v(0, 54) * mm, "end": v(1, 54) * mm});
            skLineSegment(sketch, "E27.10.0.4", {"start": v(0, 55) * mm, "end": v(5, 55) * mm});
            skLineSegment(sketch, "E27.11.0.0", {"start": v(0, 56) * mm, "end": v(1, 56) * mm});
            skLineSegment(sketch, "E27.11.0.1", {"start": v(0, 57) * mm, "end": v(1, 57) * mm});
            skLineSegment(sketch, "E27.11.0.2", {"start": v(0, 58) * mm, "end": v(1, 58) * mm});
            skLineSegment(sketch, "E27.11.0.3", {"start": v(0, 59) * mm, "end": v(1, 59) * mm});
            skLineSegment(sketch, "E27.11.0.4", {"start": v(0, 60) * mm, "end": v(5, 60) * mm});
            skLineSegment(sketch, "E27.12.0.0", {"start": v(0, 61) * mm, "end": v(1, 61) * mm});
            skLineSegment(sketch, "E27.12.0.1", {"start": v(0, 62) * mm, "end": v(1, 62) * mm});
            skLineSegment(sketch, "E27.12.0.2", {"start": v(0, 63) * mm, "end": v(1, 63) * mm});
            skLineSegment(sketch, "E27.12.0.3", {"start": v(0, 64) * mm, "end": v(1, 64) * mm});
            skLineSegment(sketch, "E27.12.0.4", {"start": v(0, 65) * mm, "end": v(5, 65) * mm});
            skLineSegment(sketch, "E27.13.0.0", {"start": v(0, 66) * mm, "end": v(1, 66) * mm});
            skLineSegment(sketch, "E27.13.0.1", {"start": v(0, 67) * mm, "end": v(1, 67) * mm});
            skLineSegment(sketch, "E27.13.0.2", {"start": v(0, 68) * mm, "end": v(1, 68) * mm});
            skLineSegment(sketch, "E27.13.0.3", {"start": v(0, 69) * mm, "end": v(1, 69) * mm});
            skLineSegment(sketch, "E27.13.0.4", {"start": v(0, 70) * mm, "end": v(5, 70) * mm});
            skLineSegment(sketch, "E27.14.0.0", {"start": v(0, 71) * mm, "end": v(1, 71) * mm});
            skLineSegment(sketch, "E27.14.0.1", {"start": v(0, 72) * mm, "end": v(1, 72) * mm});
            skLineSegment(sketch, "E27.14.0.2", {"start": v(0, 73) * mm, "end": v(1, 73) * mm});
            skLineSegment(sketch, "E27.14.0.3", {"start": v(0, 74) * mm, "end": v(1, 74) * mm});
            skLineSegment(sketch, "E27.14.0.4", {"start": v(0, 75) * mm, "end": v(5, 75) * mm});
            skLineSegment(sketch, "E27.15.0.0", {"start": v(0, 76) * mm, "end": v(1, 76) * mm});
            skLineSegment(sketch, "E27.15.0.1", {"start": v(0, 77) * mm, "end": v(1, 77) * mm});
            skLineSegment(sketch, "E27.15.0.2", {"start": v(0, 78) * mm, "end": v(1, 78) * mm});
            skLineSegment(sketch, "E27.15.0.3", {"start": v(0, 79) * mm, "end": v(1, 79) * mm});
            skLineSegment(sketch, "E27.15.0.4", {"start": v(0, 80) * mm, "end": v(5, 80) * mm});
            skLineSegment(sketch, "E27.16.0.0", {"start": v(0, 81) * mm, "end": v(1, 81) * mm});
            skLineSegment(sketch, "E27.16.0.1", {"start": v(0, 82) * mm, "end": v(1, 82) * mm});
            skLineSegment(sketch, "E27.16.0.2", {"start": v(0, 83) * mm, "end": v(1, 83) * mm});
            skLineSegment(sketch, "E27.16.0.3", {"start": v(0, 84) * mm, "end": v(1, 84) * mm});
            skLineSegment(sketch, "E27.16.0.4", {"start": v(0, 85) * mm, "end": v(5, 85) * mm});
            skLineSegment(sketch, "E27.17.0.0", {"start": v(0, 86) * mm, "end": v(1, 86) * mm});
            skLineSegment(sketch, "E27.17.0.1", {"start": v(0, 87) * mm, "end": v(1, 87) * mm});
            skLineSegment(sketch, "E27.17.0.2", {"start": v(0, 88) * mm, "end": v(1, 88) * mm});
            skLineSegment(sketch, "E27.17.0.3", {"start": v(0, 89) * mm, "end": v(1, 89) * mm});
            skLineSegment(sketch, "E27.17.0.4", {"start": v(0, 90) * mm, "end": v(5, 90) * mm});
            skLineSegment(sketch, "E27.18.0.0", {"start": v(0, 91) * mm, "end": v(1, 91) * mm});
            skLineSegment(sketch, "E27.18.0.1", {"start": v(0, 92) * mm, "end": v(1, 92) * mm});
            skLineSegment(sketch, "E27.18.0.2", {"start": v(0, 93) * mm, "end": v(1, 93) * mm});
            skLineSegment(sketch, "E27.18.0.3", {"start": v(0, 94) * mm, "end": v(1, 94) * mm});
            skLineSegment(sketch, "E27.18.0.4", {"start": v(0, 95) * mm, "end": v(5, 95) * mm});
            skLineSegment(sketch, "E27.19.0.0", {"start": v(0, 96) * mm, "end": v(1, 96) * mm});
            skLineSegment(sketch, "E27.19.0.1", {"start": v(0, 97) * mm, "end": v(1, 97) * mm});
            skLineSegment(sketch, "E27.19.0.2", {"start": v(0, 98) * mm, "end": v(1, 98) * mm});
            skLineSegment(sketch, "E27.19.0.3", {"start": v(0, 99) * mm, "end": v(1, 99) * mm});
            skLineSegment(sketch, "E27.19.0.4", {"start": v(0, 100) * mm, "end": v(5, 100) * mm});
            skLineSegment(sketch, "E27.direction1", {"start": v(0, 1) * mm, "end": v(0, 6) * mm, "construction": true});
            skSolve(sketch);
        }
        {
            var Q0;
            {var subQ30=sQuery(id+"F0.wireOp",EDGE,"E1");Q0=makeQuery(id+"F0.imprint","IMPRINT",FACE,{"disambiguationData":[TD([[makeQuery(id+"F0.imprint","IMPRINT",EDGE,{"derivedFrom":subQ30}),1.0]])]});}
            var Q1;
            {var subQ1=sQuery(id+"F0.wireOp",EDGE,"E20");Q1=makeQuery(id+"F0.imprint","IMPRINT",FACE,{"disambiguationData":[TD([[makeQuery(id+"F0.imprint","IMPRINT",EDGE,{"derivedFrom":subQ1}),-1.0]])]});}
            var Q2;
            {var subQ3=sQuery(id+"F0.wireOp",EDGE,"E20");Q2=makeQuery(id+"F0.imprint","IMPRINT",FACE,{"disambiguationData":[TD([[makeQuery(id+"F0.imprint","IMPRINT",EDGE,{"derivedFrom":subQ3}),1.0]])]});}
            extrude(context, id + "F1", {"entities" : qUnion([Q0, Q1, Q2]), "oppositeDirection" : true, "depth" : 3 * mm});
        }
    });
